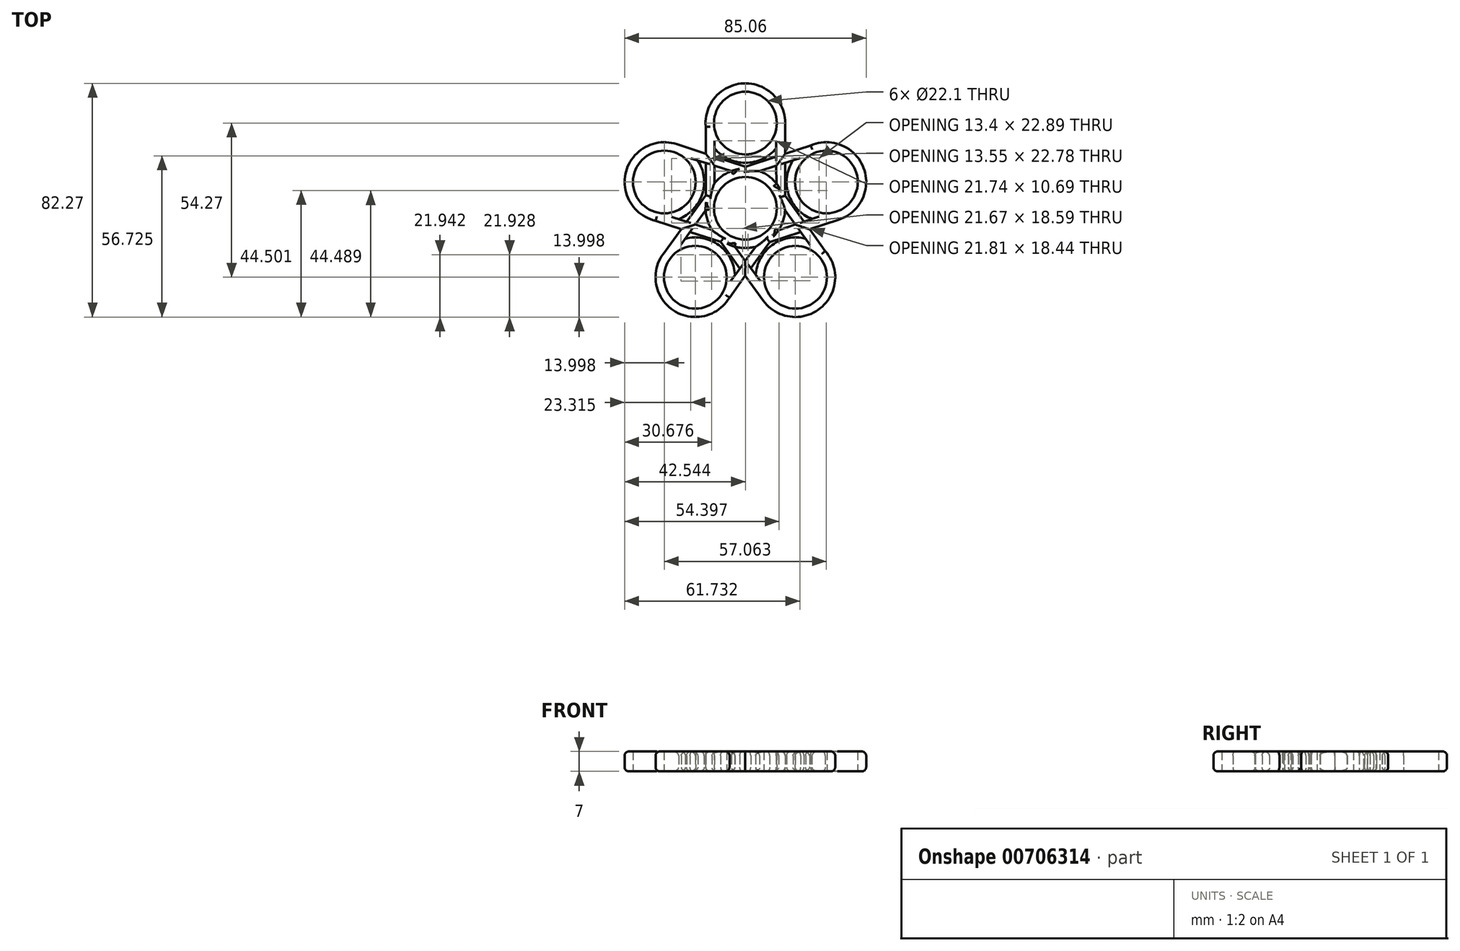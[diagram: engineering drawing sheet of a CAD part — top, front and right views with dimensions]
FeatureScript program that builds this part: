
annotation { "Feature Type Name" : "Feature", "Feature Type Description" : "" }
export const myFeature = defineFeature(function(context is Context, id is Id, definition is map)
    precondition{}
    {
        {
            var Q0;
            Q0=qCreatedBy(makeId("Top.planeOp"),FACE);
            var sketch = newSketch(context, id + "F0", { "sketchPlane" : qUnion([Q0])});
            skCircle(sketch, "E0", {"center": v(0, 22.69) * mm, "radius": 14 * mm});
            skCircle(sketch, "E1", {"center": v(0, 22.69) * mm, "radius": 11.05 * mm});
            skCircle(sketch, "E2", {"center": v(0, -7.31) * mm, "radius": 14 * mm});
            skCircle(sketch, "E3", {"center": v(0, -7.31) * mm, "radius": 11.05 * mm});
            skLineSegment(sketch, "E4", {"start": v(-13.94, 21.4) * mm, "end": v(-13.94, -8.6) * mm});
            skLineSegment(sketch, "E5", {"start": v(14, 22.69) * mm, "end": v(14, -7.31) * mm});
            skLineSegment(sketch, "E6", {"start": v(-10.85, 20.62) * mm, "end": v(-10.85, -9.38) * mm});
            skLineSegment(sketch, "E7", {"start": v(10.77, 20.22) * mm, "end": v(11.05, -7.2) * mm});
            skSolve(sketch);
        }
        {
            var Q0;
            {var subQ0=sQuery(id+"F0.wireOp",EDGE,"E0");var subQ4=makeQuery(id+"F0.imprint","INTERSECT",VERTEX,{"derivedFrom":[subQ0,sQuery(id+"F0.wireOp",EDGE,"E4")]});Q0=makeQuery(id+"F0.imprint","IMPRINT",FACE,{"disambiguationData":[TD([[makeQuery(id+"F0.imprint","IMPRINT",EDGE,{"disambiguationData":[TD([[subQ4,1.0]])],"derivedFrom":subQ0}),1.0]])]});}
            var Q1;
            {var subQ0=sQuery(id+"F0.wireOp",EDGE,"E6");var subQ1=sQuery(id+"F0.wireOp",EDGE,"E0");var subQ2=makeQuery(id+"F0.imprint","INTERSECT",VERTEX,{"derivedFrom":[subQ1,subQ0]});Q1=makeQuery(id+"F0.imprint","IMPRINT",FACE,{"disambiguationData":[TD([[makeQuery(id+"F0.imprint","IMPRINT",EDGE,{"disambiguationData":[TD([[subQ2,-1.0]])],"derivedFrom":subQ1}),1.0]])]});}
            var Q2;
            {var subQ0=sQuery(id+"F0.wireOp",EDGE,"E7");var subQ1=sQuery(id+"F0.wireOp",EDGE,"E2");var subQ2=makeQuery(id+"F0.imprint","INTERSECT",VERTEX,{"derivedFrom":[subQ1,subQ0]});Q2=makeQuery(id+"F0.imprint","IMPRINT",FACE,{"disambiguationData":[TD([[makeQuery(id+"F0.imprint","IMPRINT",EDGE,{"disambiguationData":[TD([[subQ2,-1.0]])],"derivedFrom":subQ1}),1.0]])]});}
            var Q3;
            {var subQ6=sQuery(id+"F0.wireOp",EDGE,"E2");var subQ10=makeQuery(id+"F0.imprint","INTERSECT",VERTEX,{"derivedFrom":[subQ6,sQuery(id+"F0.wireOp",EDGE,"E5")]});Q3=makeQuery(id+"F0.imprint","IMPRINT",FACE,{"disambiguationData":[TD([[makeQuery(id+"F0.imprint","IMPRINT",EDGE,{"disambiguationData":[TD([[subQ10,-1.0]])],"derivedFrom":subQ6}),1.0]])]});}
            var Q4;
            {var subQ0=sQuery(id+"F0.wireOp",EDGE,"E5");Q4=makeQuery(id+"F0.imprint","IMPRINT",FACE,{"disambiguationData":[TD([[makeQuery(id+"F0.imprint","IMPRINT",EDGE,{"derivedFrom":subQ0}),-1.0]])]});}
            var Q5;
            {var subQ0=sQuery(id+"F0.wireOp",EDGE,"E4");var subQ1=sQuery(id+"F0.wireOp",EDGE,"E0");var subQ2=makeQuery(id+"F0.imprint","INTERSECT",VERTEX,{"derivedFrom":[subQ1,subQ0]});Q5=makeQuery(id+"F0.imprint","IMPRINT",FACE,{"disambiguationData":[TD([[makeQuery(id+"F0.imprint","IMPRINT",EDGE,{"disambiguationData":[TD([[subQ2,-1.0]])],"derivedFrom":subQ1}),-1.0]])]});}
            extrude(context, id + "F1", {"entities" : qUnion([Q0, Q1, Q2, Q3, Q4, Q5]), "depth" : 7 * mm, "offsetDistance" : 25 * mm});
        }
        {
            var Q0;
            Q0=makeQuery(id+"F1.opExtrude","SWEPT_BODY",BODY,{"disambiguationData":[OSD([sQuery(id+"F0.wireOp",EDGE,"E0"),sQuery(id+"F0.wireOp",EDGE,"E1"),sQuery(id+"F0.wireOp",EDGE,"E2"),sQuery(id+"F0.wireOp",EDGE,"E3"),sQuery(id+"F0.wireOp",EDGE,"E4"),sQuery(id+"F0.wireOp",EDGE,"E5"),sQuery(id+"F0.wireOp",EDGE,"E6"),sQuery(id+"F0.wireOp",EDGE,"E7")])]});
            var Q1;
            {var subQ0=sQuery(id+"F0.wireOp",EDGE,"E2");Q1=makeQuery(id+"F1.opExtrude","SWEPT_FACE",FACE,{"disambiguationData":[OSD([subQ0]),TDD([makeQuery(id+"F0.imprint","IMPRINT",EDGE,{"disambiguationData":[TD([[makeQuery(id+"F0.imprint","INTERSECT",VERTEX,{"disambiguationData":[OD(0.0)],"derivedFrom":[subQ0,sQuery(id+"F0.wireOp",EDGE,"E4")]}),-1.0]])],"derivedFrom":subQ0})])]});}
            circularPattern(context, id + "F2", {"entities" : qUnion([Q0]), "axis" : qUnion([Q1]), "angle" : 360 * degree, "instanceCount" : 5, "equalSpace" : true});
        }
        {
            var Q0;
            Q0=makeQuery(id+"F1.opExtrude","SWEPT_BODY",BODY,{"disambiguationData":[OSD([sQuery(id+"F0.wireOp",EDGE,"E0"),sQuery(id+"F0.wireOp",EDGE,"E1"),sQuery(id+"F0.wireOp",EDGE,"E2"),sQuery(id+"F0.wireOp",EDGE,"E3"),sQuery(id+"F0.wireOp",EDGE,"E4"),sQuery(id+"F0.wireOp",EDGE,"E5"),sQuery(id+"F0.wireOp",EDGE,"E6"),sQuery(id+"F0.wireOp",EDGE,"E7")])]});
            var Q1;
            Q1=makeQuery(id+"F2.opPattern","COPY",BODY,{"derivedFrom":makeQuery(id+"F1.opExtrude","SWEPT_BODY",BODY,{"disambiguationData":[OSD([sQuery(id+"F0.wireOp",EDGE,"E0"),sQuery(id+"F0.wireOp",EDGE,"E1"),sQuery(id+"F0.wireOp",EDGE,"E2"),sQuery(id+"F0.wireOp",EDGE,"E3"),sQuery(id+"F0.wireOp",EDGE,"E4"),sQuery(id+"F0.wireOp",EDGE,"E5"),sQuery(id+"F0.wireOp",EDGE,"E6"),sQuery(id+"F0.wireOp",EDGE,"E7")])]}),"instanceName":"1"});
            var Q2;
            Q2=makeQuery(id+"F2.opPattern","COPY",BODY,{"derivedFrom":makeQuery(id+"F1.opExtrude","SWEPT_BODY",BODY,{"disambiguationData":[OSD([sQuery(id+"F0.wireOp",EDGE,"E0"),sQuery(id+"F0.wireOp",EDGE,"E1"),sQuery(id+"F0.wireOp",EDGE,"E2"),sQuery(id+"F0.wireOp",EDGE,"E3"),sQuery(id+"F0.wireOp",EDGE,"E4"),sQuery(id+"F0.wireOp",EDGE,"E5"),sQuery(id+"F0.wireOp",EDGE,"E6"),sQuery(id+"F0.wireOp",EDGE,"E7")])]}),"instanceName":"2"});
            var Q3;
            Q3=makeQuery(id+"F2.opPattern","COPY",BODY,{"derivedFrom":makeQuery(id+"F1.opExtrude","SWEPT_BODY",BODY,{"disambiguationData":[OSD([sQuery(id+"F0.wireOp",EDGE,"E0"),sQuery(id+"F0.wireOp",EDGE,"E1"),sQuery(id+"F0.wireOp",EDGE,"E2"),sQuery(id+"F0.wireOp",EDGE,"E3"),sQuery(id+"F0.wireOp",EDGE,"E4"),sQuery(id+"F0.wireOp",EDGE,"E5"),sQuery(id+"F0.wireOp",EDGE,"E6"),sQuery(id+"F0.wireOp",EDGE,"E7")])]}),"instanceName":"3"});
            var Q4;
            Q4=makeQuery(id+"F2.opPattern","COPY",BODY,{"derivedFrom":makeQuery(id+"F1.opExtrude","SWEPT_BODY",BODY,{"disambiguationData":[OSD([sQuery(id+"F0.wireOp",EDGE,"E0"),sQuery(id+"F0.wireOp",EDGE,"E1"),sQuery(id+"F0.wireOp",EDGE,"E2"),sQuery(id+"F0.wireOp",EDGE,"E3"),sQuery(id+"F0.wireOp",EDGE,"E4"),sQuery(id+"F0.wireOp",EDGE,"E5"),sQuery(id+"F0.wireOp",EDGE,"E6"),sQuery(id+"F0.wireOp",EDGE,"E7")])]}),"instanceName":"4"});
            var Q5;
            Q5=makeQuery(id+"F2.opPattern","COPY",BODY,{"derivedFrom":makeQuery(id+"F1.opExtrude","SWEPT_BODY",BODY,{"disambiguationData":[OSD([sQuery(id+"F0.wireOp",EDGE,"E0"),sQuery(id+"F0.wireOp",EDGE,"E1"),sQuery(id+"F0.wireOp",EDGE,"E2"),sQuery(id+"F0.wireOp",EDGE,"E3"),sQuery(id+"F0.wireOp",EDGE,"E4"),sQuery(id+"F0.wireOp",EDGE,"E5"),sQuery(id+"F0.wireOp",EDGE,"E6"),sQuery(id+"F0.wireOp",EDGE,"E7")])]}),"instanceName":"5"});
            booleanBodies(context, id + "F3", {"operationType" : BooleanOperationType.UNION, "tools" : qUnion([Q0, Q1, Q2, Q3, Q4, Q5])});
        }
        {
            var Q0;
            {var subQ0=sQuery(id+"F0.wireOp",EDGE,"E5");var subQ1=sQuery(id+"F0.wireOp",EDGE,"E4");Q0=makeQuery(id+"F3.opBoolean","SPLIT",EDGE,{"disambiguationData":[TD([makeQuery(id+"F2.opPattern","COPY",FACE,{"derivedFrom":makeQuery(id+"F1.opExtrude","SWEPT_FACE",FACE,{"disambiguationData":[OSD([subQ0])]}),"instanceName":"4"})])],"derivedFrom":makeQuery(id+"F1.opExtrude","CAP_EDGE",EDGE,{"disambiguationData":[OSD([subQ1])],"isStart":false})});}
            var Q1;
            {var subQ0=sQuery(id+"F0.wireOp",EDGE,"E0");Q1=makeQuery(id+"F1.opExtrude","CAP_EDGE",EDGE,{"disambiguationData":[OSD([subQ0]),TDD([makeQuery(id+"F0.imprint","IMPRINT",EDGE,{"disambiguationData":[TD([[makeQuery(id+"F0.imprint","INTERSECT",VERTEX,{"derivedFrom":[subQ0,sQuery(id+"F0.wireOp",EDGE,"E4")]}),1.0]])],"derivedFrom":subQ0})])],"isStart":false});}
            var Q2;
            {var subQ0=sQuery(id+"F0.wireOp",EDGE,"E0");Q2=makeQuery(id+"F1.opExtrude","CAP_EDGE",EDGE,{"disambiguationData":[OSD([subQ0]),TDD([makeQuery(id+"F0.imprint","IMPRINT",EDGE,{"disambiguationData":[TD([[makeQuery(id+"F0.imprint","INTERSECT",VERTEX,{"derivedFrom":[subQ0,sQuery(id+"F0.wireOp",EDGE,"E6")]}),-1.0]])],"derivedFrom":subQ0})])],"isStart":false});}
            var Q3;
            {var subQ1=sQuery(id+"F0.wireOp",EDGE,"E6");var subQ2=sQuery(id+"F0.wireOp",EDGE,"E5");Q3=makeQuery(id+"F3.opBoolean","SPLIT",EDGE,{"disambiguationData":[TD([makeQuery(id+"F1.opExtrude","SWEPT_FACE",FACE,{"disambiguationData":[OSD([subQ1])]})])],"derivedFrom":makeQuery(id+"F2.opPattern","COPY",EDGE,{"derivedFrom":makeQuery(id+"F1.opExtrude","CAP_EDGE",EDGE,{"disambiguationData":[OSD([subQ2])],"isStart":false}),"instanceName":"4"})});}
            var Q4;
            {var subQ0=sQuery(id+"F0.wireOp",EDGE,"E4");var subQ1=sQuery(id+"F0.wireOp",EDGE,"E7");Q4=makeQuery(id+"F3.opBoolean","SPLIT",EDGE,{"disambiguationData":[TD([makeQuery(id+"F1.opExtrude","SWEPT_FACE",FACE,{"disambiguationData":[OSD([subQ1])]})])],"derivedFrom":makeQuery(id+"F2.opPattern","COPY",EDGE,{"derivedFrom":makeQuery(id+"F1.opExtrude","CAP_EDGE",EDGE,{"disambiguationData":[OSD([subQ0])],"isStart":false}),"instanceName":"1"})});}
            var Q5;
            {var subQ0=sQuery(id+"F0.wireOp",EDGE,"E5");var subQ1=sQuery(id+"F0.wireOp",EDGE,"E4");Q5=makeQuery(id+"F3.opBoolean","SPLIT",EDGE,{"disambiguationData":[TD([makeQuery(id+"F1.opExtrude","SWEPT_FACE",FACE,{"disambiguationData":[OSD([subQ0])]})])],"derivedFrom":makeQuery(id+"F2.opPattern","COPY",EDGE,{"derivedFrom":makeQuery(id+"F1.opExtrude","CAP_EDGE",EDGE,{"disambiguationData":[OSD([subQ1])],"isStart":false}),"instanceName":"1"})});}
            var Q6;
            {var subQ0=sQuery(id+"F0.wireOp",EDGE,"E0");Q6=makeQuery(id+"F2.opPattern","COPY",EDGE,{"derivedFrom":makeQuery(id+"F1.opExtrude","CAP_EDGE",EDGE,{"disambiguationData":[OSD([subQ0]),TDD([makeQuery(id+"F0.imprint","IMPRINT",EDGE,{"disambiguationData":[TD([[makeQuery(id+"F0.imprint","INTERSECT",VERTEX,{"derivedFrom":[subQ0,sQuery(id+"F0.wireOp",EDGE,"E4")]}),1.0]])],"derivedFrom":subQ0})])],"isStart":false}),"instanceName":"1"});}
            var Q7;
            {var subQ0=sQuery(id+"F0.wireOp",EDGE,"E0");Q7=makeQuery(id+"F2.opPattern","COPY",EDGE,{"derivedFrom":makeQuery(id+"F1.opExtrude","CAP_EDGE",EDGE,{"disambiguationData":[OSD([subQ0]),TDD([makeQuery(id+"F0.imprint","IMPRINT",EDGE,{"disambiguationData":[TD([[makeQuery(id+"F0.imprint","INTERSECT",VERTEX,{"derivedFrom":[subQ0,sQuery(id+"F0.wireOp",EDGE,"E6")]}),-1.0]])],"derivedFrom":subQ0})])],"isStart":false}),"instanceName":"1"});}
            var Q8;
            {var subQ0=sQuery(id+"F0.wireOp",EDGE,"E6");var subQ1=sQuery(id+"F0.wireOp",EDGE,"E5");Q8=makeQuery(id+"F3.opBoolean","SPLIT",EDGE,{"disambiguationData":[TD([makeQuery(id+"F2.opPattern","COPY",FACE,{"derivedFrom":makeQuery(id+"F1.opExtrude","SWEPT_FACE",FACE,{"disambiguationData":[OSD([subQ0])]}),"instanceName":"1"})])],"derivedFrom":makeQuery(id+"F1.opExtrude","CAP_EDGE",EDGE,{"disambiguationData":[OSD([subQ1])],"isStart":false})});}
            var Q9;
            {var subQ1=sQuery(id+"F0.wireOp",EDGE,"E5");var subQ2=sQuery(id+"F0.wireOp",EDGE,"E4");Q9=makeQuery(id+"F3.opBoolean","SPLIT",EDGE,{"disambiguationData":[TD([makeQuery(id+"F1.opExtrude","SWEPT_FACE",FACE,{"disambiguationData":[OSD([subQ1])]})])],"derivedFrom":makeQuery(id+"F2.opPattern","COPY",EDGE,{"derivedFrom":makeQuery(id+"F1.opExtrude","CAP_EDGE",EDGE,{"disambiguationData":[OSD([subQ2])],"isStart":false}),"instanceName":"2"})});}
            var Q10;
            {var subQ0=sQuery(id+"F0.wireOp",EDGE,"E7");var subQ1=sQuery(id+"F0.wireOp",EDGE,"E6");Q10=makeQuery(id+"F3.opBoolean","SPLIT",EDGE,{"disambiguationData":[TD([makeQuery(id+"F2.opPattern","COPY",FACE,{"derivedFrom":makeQuery(id+"F1.opExtrude","SWEPT_FACE",FACE,{"disambiguationData":[OSD([subQ0])]}),"instanceName":"4"})])],"derivedFrom":makeQuery(id+"F1.opExtrude","CAP_EDGE",EDGE,{"disambiguationData":[OSD([subQ1])],"isStart":false})});}
            var Q11;
            {var subQ0=sQuery(id+"F0.wireOp",EDGE,"E7");var subQ1=sQuery(id+"F0.wireOp",EDGE,"E6");Q11=makeQuery(id+"F3.opBoolean","SPLIT",EDGE,{"disambiguationData":[TD([makeQuery(id+"F1.opExtrude","SWEPT_FACE",FACE,{"disambiguationData":[OSD([subQ1])]})])],"derivedFrom":makeQuery(id+"F2.opPattern","COPY",EDGE,{"derivedFrom":makeQuery(id+"F1.opExtrude","CAP_EDGE",EDGE,{"disambiguationData":[OSD([subQ0])],"isStart":false}),"instanceName":"4"})});}
            var Q12;
            {var subQ0=sQuery(id+"F0.wireOp",EDGE,"E7");var subQ1=sQuery(id+"F0.wireOp",EDGE,"E6");Q12=makeQuery(id+"F3.opBoolean","SPLIT",EDGE,{"disambiguationData":[TD([makeQuery(id+"F1.opExtrude","SWEPT_FACE",FACE,{"disambiguationData":[OSD([subQ0])]})])],"derivedFrom":makeQuery(id+"F2.opPattern","COPY",EDGE,{"derivedFrom":makeQuery(id+"F1.opExtrude","CAP_EDGE",EDGE,{"disambiguationData":[OSD([subQ1])],"isStart":false}),"instanceName":"1"})});}
            var Q13;
            {var subQ0=sQuery(id+"F0.wireOp",EDGE,"E7");var subQ1=sQuery(id+"F0.wireOp",EDGE,"E6");Q13=makeQuery(id+"F3.opBoolean","SPLIT",EDGE,{"disambiguationData":[TD([makeQuery(id+"F2.opPattern","COPY",FACE,{"derivedFrom":makeQuery(id+"F1.opExtrude","SWEPT_FACE",FACE,{"disambiguationData":[OSD([subQ1])]}),"instanceName":"1"})])],"derivedFrom":makeQuery(id+"F1.opExtrude","CAP_EDGE",EDGE,{"disambiguationData":[OSD([subQ0])],"isStart":false})});}
            var Q14;
            {var subQ0=sQuery(id+"F0.wireOp",EDGE,"E7");var subQ1=sQuery(id+"F0.wireOp",EDGE,"E6");Q14=makeQuery(id+"F3.opBoolean","SPLIT",EDGE,{"disambiguationData":[TD([makeQuery(id+"F2.opPattern","COPY",FACE,{"derivedFrom":makeQuery(id+"F1.opExtrude","SWEPT_FACE",FACE,{"disambiguationData":[OSD([subQ0])]}),"instanceName":"1"})])],"derivedFrom":makeQuery(id+"F2.opPattern","COPY",EDGE,{"derivedFrom":makeQuery(id+"F1.opExtrude","CAP_EDGE",EDGE,{"disambiguationData":[OSD([subQ1])],"isStart":false}),"instanceName":"2"})});}
            var Q15;
            {var subQ0=sQuery(id+"F0.wireOp",EDGE,"E7");var subQ1=sQuery(id+"F0.wireOp",EDGE,"E6");Q15=makeQuery(id+"F3.opBoolean","SPLIT",EDGE,{"disambiguationData":[TD([makeQuery(id+"F2.opPattern","COPY",FACE,{"derivedFrom":makeQuery(id+"F1.opExtrude","SWEPT_FACE",FACE,{"disambiguationData":[OSD([subQ1])]}),"instanceName":"2"})])],"derivedFrom":makeQuery(id+"F2.opPattern","COPY",EDGE,{"derivedFrom":makeQuery(id+"F1.opExtrude","CAP_EDGE",EDGE,{"disambiguationData":[OSD([subQ0])],"isStart":false}),"instanceName":"1"})});}
            var Q16;
            {var subQ0=sQuery(id+"F0.wireOp",EDGE,"E7");var subQ1=sQuery(id+"F0.wireOp",EDGE,"E6");Q16=makeQuery(id+"F3.opBoolean","SPLIT",EDGE,{"disambiguationData":[TD([makeQuery(id+"F2.opPattern","COPY",FACE,{"derivedFrom":makeQuery(id+"F1.opExtrude","SWEPT_FACE",FACE,{"disambiguationData":[OSD([subQ1])]}),"instanceName":"4"})])],"derivedFrom":makeQuery(id+"F2.opPattern","COPY",EDGE,{"derivedFrom":makeQuery(id+"F1.opExtrude","CAP_EDGE",EDGE,{"disambiguationData":[OSD([subQ0])],"isStart":false}),"instanceName":"3"})});}
            var Q17;
            {var subQ0=sQuery(id+"F0.wireOp",EDGE,"E7");var subQ1=sQuery(id+"F0.wireOp",EDGE,"E6");Q17=makeQuery(id+"F3.opBoolean","SPLIT",EDGE,{"disambiguationData":[TD([makeQuery(id+"F2.opPattern","COPY",FACE,{"derivedFrom":makeQuery(id+"F1.opExtrude","SWEPT_FACE",FACE,{"disambiguationData":[OSD([subQ0])]}),"instanceName":"3"})])],"derivedFrom":makeQuery(id+"F2.opPattern","COPY",EDGE,{"derivedFrom":makeQuery(id+"F1.opExtrude","CAP_EDGE",EDGE,{"disambiguationData":[OSD([subQ1])],"isStart":false}),"instanceName":"4"})});}
            var Q18;
            {var subQ0=sQuery(id+"F0.wireOp",EDGE,"E7");var subQ1=sQuery(id+"F0.wireOp",EDGE,"E6");Q18=makeQuery(id+"F3.opBoolean","SPLIT",EDGE,{"disambiguationData":[TD([makeQuery(id+"F2.opPattern","COPY",FACE,{"derivedFrom":makeQuery(id+"F1.opExtrude","SWEPT_FACE",FACE,{"disambiguationData":[OSD([subQ1])]}),"instanceName":"3"})])],"derivedFrom":makeQuery(id+"F2.opPattern","COPY",EDGE,{"derivedFrom":makeQuery(id+"F1.opExtrude","CAP_EDGE",EDGE,{"disambiguationData":[OSD([subQ0])],"isStart":false}),"instanceName":"2"})});}
            var Q19;
            {var subQ0=sQuery(id+"F0.wireOp",EDGE,"E7");var subQ1=sQuery(id+"F0.wireOp",EDGE,"E6");Q19=makeQuery(id+"F3.opBoolean","SPLIT",EDGE,{"disambiguationData":[TD([makeQuery(id+"F2.opPattern","COPY",FACE,{"derivedFrom":makeQuery(id+"F1.opExtrude","SWEPT_FACE",FACE,{"disambiguationData":[OSD([subQ0])]}),"instanceName":"2"})])],"derivedFrom":makeQuery(id+"F2.opPattern","COPY",EDGE,{"derivedFrom":makeQuery(id+"F1.opExtrude","CAP_EDGE",EDGE,{"disambiguationData":[OSD([subQ1])],"isStart":false}),"instanceName":"3"})});}
            var Q20;
            {var subQ0=sQuery(id+"F0.wireOp",EDGE,"E5");var subQ1=sQuery(id+"F0.wireOp",EDGE,"E4");Q20=makeQuery(id+"F3.opBoolean","SPLIT",EDGE,{"disambiguationData":[TD([makeQuery(id+"F2.opPattern","COPY",FACE,{"derivedFrom":makeQuery(id+"F1.opExtrude","SWEPT_FACE",FACE,{"disambiguationData":[OSD([subQ0])]}),"instanceName":"1"})])],"derivedFrom":makeQuery(id+"F2.opPattern","COPY",EDGE,{"derivedFrom":makeQuery(id+"F1.opExtrude","CAP_EDGE",EDGE,{"disambiguationData":[OSD([subQ1])],"isStart":false}),"instanceName":"2"})});}
            var Q21;
            {var subQ0=sQuery(id+"F0.wireOp",EDGE,"E0");Q21=makeQuery(id+"F2.opPattern","COPY",EDGE,{"derivedFrom":makeQuery(id+"F1.opExtrude","CAP_EDGE",EDGE,{"disambiguationData":[OSD([subQ0]),TDD([makeQuery(id+"F0.imprint","IMPRINT",EDGE,{"disambiguationData":[TD([[makeQuery(id+"F0.imprint","INTERSECT",VERTEX,{"derivedFrom":[subQ0,sQuery(id+"F0.wireOp",EDGE,"E4")]}),1.0]])],"derivedFrom":subQ0})])],"isStart":false}),"instanceName":"2"});}
            var Q22;
            {var subQ0=sQuery(id+"F0.wireOp",EDGE,"E5");var subQ1=sQuery(id+"F0.wireOp",EDGE,"E4");Q22=makeQuery(id+"F3.opBoolean","SPLIT",EDGE,{"disambiguationData":[TD([makeQuery(id+"F2.opPattern","COPY",FACE,{"derivedFrom":makeQuery(id+"F1.opExtrude","SWEPT_FACE",FACE,{"disambiguationData":[OSD([subQ0])]}),"instanceName":"2"})])],"derivedFrom":makeQuery(id+"F2.opPattern","COPY",EDGE,{"derivedFrom":makeQuery(id+"F1.opExtrude","CAP_EDGE",EDGE,{"disambiguationData":[OSD([subQ1])],"isStart":false}),"instanceName":"3"})});}
            var Q23;
            {var subQ0=sQuery(id+"F0.wireOp",EDGE,"E0");Q23=makeQuery(id+"F2.opPattern","COPY",EDGE,{"derivedFrom":makeQuery(id+"F1.opExtrude","CAP_EDGE",EDGE,{"disambiguationData":[OSD([subQ0]),TDD([makeQuery(id+"F0.imprint","IMPRINT",EDGE,{"disambiguationData":[TD([[makeQuery(id+"F0.imprint","INTERSECT",VERTEX,{"derivedFrom":[subQ0,sQuery(id+"F0.wireOp",EDGE,"E4")]}),1.0]])],"derivedFrom":subQ0})])],"isStart":false}),"instanceName":"3"});}
            var Q24;
            {var subQ0=sQuery(id+"F0.wireOp",EDGE,"E5");var subQ1=sQuery(id+"F0.wireOp",EDGE,"E4");Q24=makeQuery(id+"F3.opBoolean","SPLIT",EDGE,{"disambiguationData":[TD([makeQuery(id+"F2.opPattern","COPY",FACE,{"derivedFrom":makeQuery(id+"F1.opExtrude","SWEPT_FACE",FACE,{"disambiguationData":[OSD([subQ0])]}),"instanceName":"3"})])],"derivedFrom":makeQuery(id+"F2.opPattern","COPY",EDGE,{"derivedFrom":makeQuery(id+"F1.opExtrude","CAP_EDGE",EDGE,{"disambiguationData":[OSD([subQ1])],"isStart":false}),"instanceName":"4"})});}
            var Q25;
            {var subQ0=sQuery(id+"F0.wireOp",EDGE,"E0");Q25=makeQuery(id+"F2.opPattern","COPY",EDGE,{"derivedFrom":makeQuery(id+"F1.opExtrude","CAP_EDGE",EDGE,{"disambiguationData":[OSD([subQ0]),TDD([makeQuery(id+"F0.imprint","IMPRINT",EDGE,{"disambiguationData":[TD([[makeQuery(id+"F0.imprint","INTERSECT",VERTEX,{"derivedFrom":[subQ0,sQuery(id+"F0.wireOp",EDGE,"E4")]}),1.0]])],"derivedFrom":subQ0})])],"isStart":false}),"instanceName":"4"});}
            var Q26;
            {var subQ0=sQuery(id+"F0.wireOp",EDGE,"E0");Q26=makeQuery(id+"F2.opPattern","COPY",EDGE,{"derivedFrom":makeQuery(id+"F1.opExtrude","CAP_EDGE",EDGE,{"disambiguationData":[OSD([subQ0]),TDD([makeQuery(id+"F0.imprint","IMPRINT",EDGE,{"disambiguationData":[TD([[makeQuery(id+"F0.imprint","INTERSECT",VERTEX,{"derivedFrom":[subQ0,sQuery(id+"F0.wireOp",EDGE,"E6")]}),-1.0]])],"derivedFrom":subQ0})])],"isStart":false}),"instanceName":"4"});}
            var Q27;
            {var subQ1=sQuery(id+"F0.wireOp",EDGE,"E5");var subQ2=sQuery(id+"F0.wireOp",EDGE,"E4");Q27=makeQuery(id+"F3.opBoolean","SPLIT",EDGE,{"disambiguationData":[TD([makeQuery(id+"F2.opPattern","COPY",FACE,{"derivedFrom":makeQuery(id+"F1.opExtrude","SWEPT_FACE",FACE,{"disambiguationData":[OSD([subQ1])]}),"instanceName":"3"})])],"derivedFrom":makeQuery(id+"F1.opExtrude","CAP_EDGE",EDGE,{"disambiguationData":[OSD([subQ2])],"isStart":false})});}
            var Q28;
            {var subQ1=sQuery(id+"F0.wireOp",EDGE,"E5");var subQ2=sQuery(id+"F0.wireOp",EDGE,"E4");Q28=makeQuery(id+"F3.opBoolean","SPLIT",EDGE,{"disambiguationData":[TD([makeQuery(id+"F1.opExtrude","SWEPT_FACE",FACE,{"disambiguationData":[OSD([subQ2])]})])],"derivedFrom":makeQuery(id+"F2.opPattern","COPY",EDGE,{"derivedFrom":makeQuery(id+"F1.opExtrude","CAP_EDGE",EDGE,{"disambiguationData":[OSD([subQ1])],"isStart":false}),"instanceName":"3"})});}
            var Q29;
            {var subQ0=sQuery(id+"F0.wireOp",EDGE,"E0");Q29=makeQuery(id+"F2.opPattern","COPY",EDGE,{"derivedFrom":makeQuery(id+"F1.opExtrude","CAP_EDGE",EDGE,{"disambiguationData":[OSD([subQ0]),TDD([makeQuery(id+"F0.imprint","IMPRINT",EDGE,{"disambiguationData":[TD([[makeQuery(id+"F0.imprint","INTERSECT",VERTEX,{"derivedFrom":[subQ0,sQuery(id+"F0.wireOp",EDGE,"E6")]}),-1.0]])],"derivedFrom":subQ0})])],"isStart":false}),"instanceName":"2"});}
            var Q30;
            {var subQ1=sQuery(id+"F0.wireOp",EDGE,"E5");var subQ2=sQuery(id+"F0.wireOp",EDGE,"E4");Q30=makeQuery(id+"F3.opBoolean","SPLIT",EDGE,{"disambiguationData":[TD([makeQuery(id+"F2.opPattern","COPY",FACE,{"derivedFrom":makeQuery(id+"F1.opExtrude","SWEPT_FACE",FACE,{"disambiguationData":[OSD([subQ1])]}),"instanceName":"1"})])],"derivedFrom":makeQuery(id+"F2.opPattern","COPY",EDGE,{"derivedFrom":makeQuery(id+"F1.opExtrude","CAP_EDGE",EDGE,{"disambiguationData":[OSD([subQ2])],"isStart":false}),"instanceName":"3"})});}
            var Q31;
            {var subQ0=sQuery(id+"F0.wireOp",EDGE,"E6");var subQ1=sQuery(id+"F0.wireOp",EDGE,"E5");Q31=makeQuery(id+"F3.opBoolean","SPLIT",EDGE,{"disambiguationData":[TD([makeQuery(id+"F2.opPattern","COPY",FACE,{"derivedFrom":makeQuery(id+"F1.opExtrude","SWEPT_FACE",FACE,{"disambiguationData":[OSD([subQ0])]}),"instanceName":"2"})])],"derivedFrom":makeQuery(id+"F2.opPattern","COPY",EDGE,{"derivedFrom":makeQuery(id+"F1.opExtrude","CAP_EDGE",EDGE,{"disambiguationData":[OSD([subQ1])],"isStart":false}),"instanceName":"1"})});}
            var Q32;
            {var subQ0=sQuery(id+"F0.wireOp",EDGE,"E0");Q32=makeQuery(id+"F2.opPattern","COPY",EDGE,{"derivedFrom":makeQuery(id+"F1.opExtrude","CAP_EDGE",EDGE,{"disambiguationData":[OSD([subQ0]),TDD([makeQuery(id+"F0.imprint","IMPRINT",EDGE,{"disambiguationData":[TD([[makeQuery(id+"F0.imprint","INTERSECT",VERTEX,{"derivedFrom":[subQ0,sQuery(id+"F0.wireOp",EDGE,"E6")]}),-1.0]])],"derivedFrom":subQ0})])],"isStart":false}),"instanceName":"3"});}
            var Q33;
            {var subQ1=sQuery(id+"F0.wireOp",EDGE,"E5");var subQ2=sQuery(id+"F0.wireOp",EDGE,"E4");Q33=makeQuery(id+"F3.opBoolean","SPLIT",EDGE,{"disambiguationData":[TD([makeQuery(id+"F2.opPattern","COPY",FACE,{"derivedFrom":makeQuery(id+"F1.opExtrude","SWEPT_FACE",FACE,{"disambiguationData":[OSD([subQ1])]}),"instanceName":"2"})])],"derivedFrom":makeQuery(id+"F2.opPattern","COPY",EDGE,{"derivedFrom":makeQuery(id+"F1.opExtrude","CAP_EDGE",EDGE,{"disambiguationData":[OSD([subQ2])],"isStart":false}),"instanceName":"4"})});}
            var Q34;
            {var subQ0=sQuery(id+"F0.wireOp",EDGE,"E6");var subQ1=sQuery(id+"F0.wireOp",EDGE,"E5");Q34=makeQuery(id+"F3.opBoolean","SPLIT",EDGE,{"disambiguationData":[TD([makeQuery(id+"F2.opPattern","COPY",FACE,{"derivedFrom":makeQuery(id+"F1.opExtrude","SWEPT_FACE",FACE,{"disambiguationData":[OSD([subQ0])]}),"instanceName":"3"})])],"derivedFrom":makeQuery(id+"F2.opPattern","COPY",EDGE,{"derivedFrom":makeQuery(id+"F1.opExtrude","CAP_EDGE",EDGE,{"disambiguationData":[OSD([subQ1])],"isStart":false}),"instanceName":"2"})});}
            fillet(context, id + "F4", {"entities" : qUnion([Q0, Q1, Q2, Q3, Q4, Q5, Q6, Q7, Q8, Q9, Q10, Q11, Q12, Q13, Q14, Q15, Q16, Q17, Q18, Q19, Q20, Q21, Q22, Q23, Q24, Q25, Q26, Q27, Q28, Q29, Q30, Q31, Q32, Q33, Q34]), "radius" : 1.5 * mm, "tangentPropagation" : true, "allowEdgeOverflow" : false});
        }
        {
            var Q0;
            {var subQ0=sQuery(id+"F0.wireOp",EDGE,"E7");var subQ1=sQuery(id+"F0.wireOp",EDGE,"E6");var subQ2=sQuery(id+"F0.wireOp",EDGE,"E2");var subQ4=makeQuery(id+"F0.imprint","IMPRINT",EDGE,{"disambiguationData":[TD([[makeQuery(id+"F0.imprint","INTERSECT",VERTEX,{"derivedFrom":[subQ2,subQ0]}),-1.0]])],"derivedFrom":subQ2});Q0=makeQuery(id+"F3.opBoolean","SPLIT",EDGE,{"disambiguationData":[TD([makeQuery(id+"F1.opExtrude","SWEPT_FACE",FACE,{"disambiguationData":[OSD([subQ1])]})])],"derivedFrom":makeQuery(id+"F1.opExtrude","CAP_EDGE",EDGE,{"disambiguationData":[OSD([subQ2]),TDD([subQ4])],"isStart":false})});}
            var Q1;
            {var subQ0=sQuery(id+"F0.wireOp",EDGE,"E7");var subQ2=sQuery(id+"F0.wireOp",EDGE,"E2");var subQ4=makeQuery(id+"F0.imprint","IMPRINT",EDGE,{"disambiguationData":[TD([[makeQuery(id+"F0.imprint","INTERSECT",VERTEX,{"derivedFrom":[subQ2,subQ0]}),-1.0]])],"derivedFrom":subQ2});Q1=makeQuery(id+"F3.opBoolean","SPLIT",EDGE,{"disambiguationData":[TD([makeQuery(id+"F1.opExtrude","SWEPT_FACE",FACE,{"disambiguationData":[OSD([subQ0])]})])],"derivedFrom":makeQuery(id+"F1.opExtrude","CAP_EDGE",EDGE,{"disambiguationData":[OSD([subQ2]),TDD([subQ4])],"isStart":false})});}
            var Q2;
            {var subQ0=sQuery(id+"F0.wireOp",EDGE,"E7");var subQ3=sQuery(id+"F0.wireOp",EDGE,"E4");var subQ4=sQuery(id+"F0.wireOp",EDGE,"E2");var subQ6=makeQuery(id+"F0.imprint","IMPRINT",EDGE,{"disambiguationData":[TD([[makeQuery(id+"F0.imprint","INTERSECT",VERTEX,{"disambiguationData":[OD(0.0)],"derivedFrom":[subQ4,subQ3]}),-1.0]])],"derivedFrom":subQ4});Q2=makeQuery(id+"F3.opBoolean","SPLIT",EDGE,{"disambiguationData":[TD([makeQuery(id+"F2.opPattern","COPY",FACE,{"derivedFrom":makeQuery(id+"F1.opExtrude","SWEPT_FACE",FACE,{"disambiguationData":[OSD([subQ0])]}),"instanceName":"1"})])],"derivedFrom":makeQuery(id+"F1.opExtrude","CAP_EDGE",EDGE,{"disambiguationData":[OSD([subQ4]),TDD([subQ6])],"isStart":false})});}
            var Q3;
            {var subQ0=sQuery(id+"F0.wireOp",EDGE,"E7");var subQ3=sQuery(id+"F0.wireOp",EDGE,"E4");var subQ4=sQuery(id+"F0.wireOp",EDGE,"E2");var subQ6=makeQuery(id+"F0.imprint","IMPRINT",EDGE,{"disambiguationData":[TD([[makeQuery(id+"F0.imprint","INTERSECT",VERTEX,{"disambiguationData":[OD(0.0)],"derivedFrom":[subQ4,subQ3]}),-1.0]])],"derivedFrom":subQ4});Q3=makeQuery(id+"F3.opBoolean","SPLIT",EDGE,{"disambiguationData":[TD([makeQuery(id+"F2.opPattern","COPY",FACE,{"derivedFrom":makeQuery(id+"F1.opExtrude","SWEPT_FACE",FACE,{"disambiguationData":[OSD([subQ0])]}),"instanceName":"2"})])],"derivedFrom":makeQuery(id+"F1.opExtrude","CAP_EDGE",EDGE,{"disambiguationData":[OSD([subQ4]),TDD([subQ6])],"isStart":false})});}
            var Q4;
            {var subQ0=sQuery(id+"F0.wireOp",EDGE,"E2");var subQ1=makeQuery(id+"F1.opExtrude","CAP_EDGE",EDGE,{"disambiguationData":[OSD([subQ0]),TDD([makeQuery(id+"F0.imprint","IMPRINT",EDGE,{"disambiguationData":[TD([[makeQuery(id+"F0.imprint","INTERSECT",VERTEX,{"disambiguationData":[OD(0.0)],"derivedFrom":[subQ0,sQuery(id+"F0.wireOp",EDGE,"E4")]}),-1.0]])],"derivedFrom":subQ0})])],"isStart":false});Q4=makeQuery(id+"F3.opBoolean","MERGE",EDGE,{"derivedFrom":[subQ1,makeQuery(id+"F2.opPattern","COPY",EDGE,{"derivedFrom":subQ1,"instanceName":"1"})]});}
            fillet(context, id + "F5", {"entities" : qUnion([Q0, Q1, Q2, Q3, Q4]), "radius" : 1.2 * mm, "tangentPropagation" : true, "allowEdgeOverflow" : false});
        }
        {
            var Q0;
            {var subQ0=sQuery(id+"F0.wireOp",EDGE,"E4");var subQ2=sQuery(id+"F0.wireOp",EDGE,"E5");Q0=makeQuery(id+"F3.opBoolean","SPLIT",EDGE,{"disambiguationData":[TD([makeQuery(id+"F2.opPattern","COPY",FACE,{"derivedFrom":makeQuery(id+"F1.opExtrude","SWEPT_FACE",FACE,{"disambiguationData":[OSD([subQ0])]}),"instanceName":"4"})])],"derivedFrom":makeQuery(id+"F2.opPattern","COPY",EDGE,{"derivedFrom":makeQuery(id+"F1.opExtrude","CAP_EDGE",EDGE,{"disambiguationData":[OSD([subQ2])],"isStart":true}),"instanceName":"3"})});}
            var Q1;
            {var subQ0=sQuery(id+"F0.wireOp",EDGE,"E0");Q1=makeQuery(id+"F2.opPattern","COPY",EDGE,{"derivedFrom":makeQuery(id+"F1.opExtrude","CAP_EDGE",EDGE,{"disambiguationData":[OSD([subQ0]),TDD([makeQuery(id+"F0.imprint","IMPRINT",EDGE,{"disambiguationData":[TD([[makeQuery(id+"F0.imprint","INTERSECT",VERTEX,{"derivedFrom":[subQ0,sQuery(id+"F0.wireOp",EDGE,"E4")]}),1.0]])],"derivedFrom":subQ0})])],"isStart":true}),"instanceName":"3"});}
            var Q2;
            {var subQ0=sQuery(id+"F0.wireOp",EDGE,"E5");var subQ1=sQuery(id+"F0.wireOp",EDGE,"E4");Q2=makeQuery(id+"F3.opBoolean","SPLIT",EDGE,{"disambiguationData":[TD([makeQuery(id+"F2.opPattern","COPY",FACE,{"derivedFrom":makeQuery(id+"F1.opExtrude","SWEPT_FACE",FACE,{"disambiguationData":[OSD([subQ0])]}),"instanceName":"2"})])],"derivedFrom":makeQuery(id+"F2.opPattern","COPY",EDGE,{"derivedFrom":makeQuery(id+"F1.opExtrude","CAP_EDGE",EDGE,{"disambiguationData":[OSD([subQ1])],"isStart":true}),"instanceName":"3"})});}
            var Q3;
            {var subQ0=sQuery(id+"F0.wireOp",EDGE,"E5");var subQ1=sQuery(id+"F0.wireOp",EDGE,"E4");Q3=makeQuery(id+"F3.opBoolean","SPLIT",EDGE,{"disambiguationData":[TD([makeQuery(id+"F2.opPattern","COPY",FACE,{"derivedFrom":makeQuery(id+"F1.opExtrude","SWEPT_FACE",FACE,{"disambiguationData":[OSD([subQ1])]}),"instanceName":"3"})])],"derivedFrom":makeQuery(id+"F2.opPattern","COPY",EDGE,{"derivedFrom":makeQuery(id+"F1.opExtrude","CAP_EDGE",EDGE,{"disambiguationData":[OSD([subQ0])],"isStart":true}),"instanceName":"2"})});}
            var Q4;
            {var subQ0=sQuery(id+"F0.wireOp",EDGE,"E0");Q4=makeQuery(id+"F2.opPattern","COPY",EDGE,{"derivedFrom":makeQuery(id+"F1.opExtrude","CAP_EDGE",EDGE,{"disambiguationData":[OSD([subQ0]),TDD([makeQuery(id+"F0.imprint","IMPRINT",EDGE,{"disambiguationData":[TD([[makeQuery(id+"F0.imprint","INTERSECT",VERTEX,{"derivedFrom":[subQ0,sQuery(id+"F0.wireOp",EDGE,"E4")]}),1.0]])],"derivedFrom":subQ0})])],"isStart":true}),"instanceName":"2"});}
            var Q5;
            {var subQ0=sQuery(id+"F0.wireOp",EDGE,"E4");var subQ2=sQuery(id+"F0.wireOp",EDGE,"E5");Q5=makeQuery(id+"F3.opBoolean","SPLIT",EDGE,{"disambiguationData":[TD([makeQuery(id+"F2.opPattern","COPY",FACE,{"derivedFrom":makeQuery(id+"F1.opExtrude","SWEPT_FACE",FACE,{"disambiguationData":[OSD([subQ2])]}),"instanceName":"1"})])],"derivedFrom":makeQuery(id+"F2.opPattern","COPY",EDGE,{"derivedFrom":makeQuery(id+"F1.opExtrude","CAP_EDGE",EDGE,{"disambiguationData":[OSD([subQ0])],"isStart":true}),"instanceName":"2"})});}
            var Q6;
            {var subQ0=sQuery(id+"F0.wireOp",EDGE,"E5");var subQ1=sQuery(id+"F0.wireOp",EDGE,"E4");Q6=makeQuery(id+"F3.opBoolean","SPLIT",EDGE,{"disambiguationData":[TD([makeQuery(id+"F2.opPattern","COPY",FACE,{"derivedFrom":makeQuery(id+"F1.opExtrude","SWEPT_FACE",FACE,{"disambiguationData":[OSD([subQ1])]}),"instanceName":"2"})])],"derivedFrom":makeQuery(id+"F2.opPattern","COPY",EDGE,{"derivedFrom":makeQuery(id+"F1.opExtrude","CAP_EDGE",EDGE,{"disambiguationData":[OSD([subQ0])],"isStart":true}),"instanceName":"1"})});}
            var Q7;
            {var subQ0=sQuery(id+"F0.wireOp",EDGE,"E0");Q7=makeQuery(id+"F2.opPattern","COPY",EDGE,{"derivedFrom":makeQuery(id+"F1.opExtrude","CAP_EDGE",EDGE,{"disambiguationData":[OSD([subQ0]),TDD([makeQuery(id+"F0.imprint","IMPRINT",EDGE,{"disambiguationData":[TD([[makeQuery(id+"F0.imprint","INTERSECT",VERTEX,{"derivedFrom":[subQ0,sQuery(id+"F0.wireOp",EDGE,"E4")]}),1.0]])],"derivedFrom":subQ0})])],"isStart":true}),"instanceName":"1"});}
            var Q8;
            {var subQ0=sQuery(id+"F0.wireOp",EDGE,"E5");var subQ1=sQuery(id+"F0.wireOp",EDGE,"E4");Q8=makeQuery(id+"F3.opBoolean","SPLIT",EDGE,{"disambiguationData":[TD([makeQuery(id+"F1.opExtrude","SWEPT_FACE",FACE,{"disambiguationData":[OSD([subQ0])]})])],"derivedFrom":makeQuery(id+"F2.opPattern","COPY",EDGE,{"derivedFrom":makeQuery(id+"F1.opExtrude","CAP_EDGE",EDGE,{"disambiguationData":[OSD([subQ1])],"isStart":true}),"instanceName":"1"})});}
            var Q9;
            {var subQ0=sQuery(id+"F0.wireOp",EDGE,"E5");var subQ1=sQuery(id+"F0.wireOp",EDGE,"E4");Q9=makeQuery(id+"F3.opBoolean","SPLIT",EDGE,{"disambiguationData":[TD([makeQuery(id+"F2.opPattern","COPY",FACE,{"derivedFrom":makeQuery(id+"F1.opExtrude","SWEPT_FACE",FACE,{"disambiguationData":[OSD([subQ0])]}),"instanceName":"3"})])],"derivedFrom":makeQuery(id+"F2.opPattern","COPY",EDGE,{"derivedFrom":makeQuery(id+"F1.opExtrude","CAP_EDGE",EDGE,{"disambiguationData":[OSD([subQ1])],"isStart":true}),"instanceName":"4"})});}
            var Q10;
            {var subQ0=sQuery(id+"F0.wireOp",EDGE,"E0");Q10=makeQuery(id+"F2.opPattern","COPY",EDGE,{"derivedFrom":makeQuery(id+"F1.opExtrude","CAP_EDGE",EDGE,{"disambiguationData":[OSD([subQ0]),TDD([makeQuery(id+"F0.imprint","IMPRINT",EDGE,{"disambiguationData":[TD([[makeQuery(id+"F0.imprint","INTERSECT",VERTEX,{"derivedFrom":[subQ0,sQuery(id+"F0.wireOp",EDGE,"E4")]}),1.0]])],"derivedFrom":subQ0})])],"isStart":true}),"instanceName":"4"});}
            var Q11;
            {var subQ0=sQuery(id+"F0.wireOp",EDGE,"E0");Q11=makeQuery(id+"F1.opExtrude","CAP_EDGE",EDGE,{"disambiguationData":[OSD([subQ0]),TDD([makeQuery(id+"F0.imprint","IMPRINT",EDGE,{"disambiguationData":[TD([[makeQuery(id+"F0.imprint","INTERSECT",VERTEX,{"derivedFrom":[subQ0,sQuery(id+"F0.wireOp",EDGE,"E4")]}),1.0]])],"derivedFrom":subQ0})])],"isStart":true});}
            var Q12;
            {var subQ0=sQuery(id+"F0.wireOp",EDGE,"E5");var subQ1=sQuery(id+"F0.wireOp",EDGE,"E4");Q12=makeQuery(id+"F3.opBoolean","SPLIT",EDGE,{"disambiguationData":[TD([makeQuery(id+"F2.opPattern","COPY",FACE,{"derivedFrom":makeQuery(id+"F1.opExtrude","SWEPT_FACE",FACE,{"disambiguationData":[OSD([subQ0])]}),"instanceName":"4"})])],"derivedFrom":makeQuery(id+"F1.opExtrude","CAP_EDGE",EDGE,{"disambiguationData":[OSD([subQ1])],"isStart":true})});}
            var Q13;
            {var subQ0=sQuery(id+"F0.wireOp",EDGE,"E0");Q13=makeQuery(id+"F2.opPattern","COPY",EDGE,{"derivedFrom":makeQuery(id+"F1.opExtrude","CAP_EDGE",EDGE,{"disambiguationData":[OSD([subQ0]),TDD([makeQuery(id+"F0.imprint","IMPRINT",EDGE,{"disambiguationData":[TD([[makeQuery(id+"F0.imprint","INTERSECT",VERTEX,{"derivedFrom":[subQ0,sQuery(id+"F0.wireOp",EDGE,"E6")]}),-1.0]])],"derivedFrom":subQ0})])],"isStart":true}),"instanceName":"3"});}
            var Q14;
            {var subQ1=sQuery(id+"F0.wireOp",EDGE,"E5");var subQ2=sQuery(id+"F0.wireOp",EDGE,"E4");Q14=makeQuery(id+"F3.opBoolean","SPLIT",EDGE,{"disambiguationData":[TD([makeQuery(id+"F2.opPattern","COPY",FACE,{"derivedFrom":makeQuery(id+"F1.opExtrude","SWEPT_FACE",FACE,{"disambiguationData":[OSD([subQ1])]}),"instanceName":"2"})])],"derivedFrom":makeQuery(id+"F2.opPattern","COPY",EDGE,{"derivedFrom":makeQuery(id+"F1.opExtrude","CAP_EDGE",EDGE,{"disambiguationData":[OSD([subQ2])],"isStart":true}),"instanceName":"4"})});}
            var Q15;
            {var subQ0=sQuery(id+"F0.wireOp",EDGE,"E6");var subQ1=sQuery(id+"F0.wireOp",EDGE,"E5");Q15=makeQuery(id+"F3.opBoolean","SPLIT",EDGE,{"disambiguationData":[TD([makeQuery(id+"F2.opPattern","COPY",FACE,{"derivedFrom":makeQuery(id+"F1.opExtrude","SWEPT_FACE",FACE,{"disambiguationData":[OSD([subQ0])]}),"instanceName":"3"})])],"derivedFrom":makeQuery(id+"F2.opPattern","COPY",EDGE,{"derivedFrom":makeQuery(id+"F1.opExtrude","CAP_EDGE",EDGE,{"disambiguationData":[OSD([subQ1])],"isStart":true}),"instanceName":"2"})});}
            var Q16;
            {var subQ0=sQuery(id+"F0.wireOp",EDGE,"E0");Q16=makeQuery(id+"F2.opPattern","COPY",EDGE,{"derivedFrom":makeQuery(id+"F1.opExtrude","CAP_EDGE",EDGE,{"disambiguationData":[OSD([subQ0]),TDD([makeQuery(id+"F0.imprint","IMPRINT",EDGE,{"disambiguationData":[TD([[makeQuery(id+"F0.imprint","INTERSECT",VERTEX,{"derivedFrom":[subQ0,sQuery(id+"F0.wireOp",EDGE,"E6")]}),-1.0]])],"derivedFrom":subQ0})])],"isStart":true}),"instanceName":"2"});}
            var Q17;
            {var subQ1=sQuery(id+"F0.wireOp",EDGE,"E5");var subQ2=sQuery(id+"F0.wireOp",EDGE,"E4");Q17=makeQuery(id+"F3.opBoolean","SPLIT",EDGE,{"disambiguationData":[TD([makeQuery(id+"F2.opPattern","COPY",FACE,{"derivedFrom":makeQuery(id+"F1.opExtrude","SWEPT_FACE",FACE,{"disambiguationData":[OSD([subQ1])]}),"instanceName":"1"})])],"derivedFrom":makeQuery(id+"F2.opPattern","COPY",EDGE,{"derivedFrom":makeQuery(id+"F1.opExtrude","CAP_EDGE",EDGE,{"disambiguationData":[OSD([subQ2])],"isStart":true}),"instanceName":"3"})});}
            var Q18;
            {var subQ0=sQuery(id+"F0.wireOp",EDGE,"E6");var subQ1=sQuery(id+"F0.wireOp",EDGE,"E5");Q18=makeQuery(id+"F3.opBoolean","SPLIT",EDGE,{"disambiguationData":[TD([makeQuery(id+"F2.opPattern","COPY",FACE,{"derivedFrom":makeQuery(id+"F1.opExtrude","SWEPT_FACE",FACE,{"disambiguationData":[OSD([subQ0])]}),"instanceName":"2"})])],"derivedFrom":makeQuery(id+"F2.opPattern","COPY",EDGE,{"derivedFrom":makeQuery(id+"F1.opExtrude","CAP_EDGE",EDGE,{"disambiguationData":[OSD([subQ1])],"isStart":true}),"instanceName":"1"})});}
            var Q19;
            {var subQ1=sQuery(id+"F0.wireOp",EDGE,"E5");var subQ2=sQuery(id+"F0.wireOp",EDGE,"E4");Q19=makeQuery(id+"F3.opBoolean","SPLIT",EDGE,{"disambiguationData":[TD([makeQuery(id+"F1.opExtrude","SWEPT_FACE",FACE,{"disambiguationData":[OSD([subQ1])]})])],"derivedFrom":makeQuery(id+"F2.opPattern","COPY",EDGE,{"derivedFrom":makeQuery(id+"F1.opExtrude","CAP_EDGE",EDGE,{"disambiguationData":[OSD([subQ2])],"isStart":true}),"instanceName":"2"})});}
            var Q20;
            {var subQ0=sQuery(id+"F0.wireOp",EDGE,"E6");var subQ1=sQuery(id+"F0.wireOp",EDGE,"E5");Q20=makeQuery(id+"F3.opBoolean","SPLIT",EDGE,{"disambiguationData":[TD([makeQuery(id+"F2.opPattern","COPY",FACE,{"derivedFrom":makeQuery(id+"F1.opExtrude","SWEPT_FACE",FACE,{"disambiguationData":[OSD([subQ0])]}),"instanceName":"1"})])],"derivedFrom":makeQuery(id+"F1.opExtrude","CAP_EDGE",EDGE,{"disambiguationData":[OSD([subQ1])],"isStart":true})});}
            var Q21;
            {var subQ0=sQuery(id+"F0.wireOp",EDGE,"E0");Q21=makeQuery(id+"F2.opPattern","COPY",EDGE,{"derivedFrom":makeQuery(id+"F1.opExtrude","CAP_EDGE",EDGE,{"disambiguationData":[OSD([subQ0]),TDD([makeQuery(id+"F0.imprint","IMPRINT",EDGE,{"disambiguationData":[TD([[makeQuery(id+"F0.imprint","INTERSECT",VERTEX,{"derivedFrom":[subQ0,sQuery(id+"F0.wireOp",EDGE,"E6")]}),-1.0]])],"derivedFrom":subQ0})])],"isStart":true}),"instanceName":"1"});}
            var Q22;
            {var subQ0=sQuery(id+"F0.wireOp",EDGE,"E0");Q22=makeQuery(id+"F1.opExtrude","CAP_EDGE",EDGE,{"disambiguationData":[OSD([subQ0]),TDD([makeQuery(id+"F0.imprint","IMPRINT",EDGE,{"disambiguationData":[TD([[makeQuery(id+"F0.imprint","INTERSECT",VERTEX,{"derivedFrom":[subQ0,sQuery(id+"F0.wireOp",EDGE,"E6")]}),-1.0]])],"derivedFrom":subQ0})])],"isStart":true});}
            var Q23;
            {var subQ0=sQuery(id+"F0.wireOp",EDGE,"E4");var subQ1=sQuery(id+"F0.wireOp",EDGE,"E7");Q23=makeQuery(id+"F3.opBoolean","SPLIT",EDGE,{"disambiguationData":[TD([makeQuery(id+"F1.opExtrude","SWEPT_FACE",FACE,{"disambiguationData":[OSD([subQ1])]})])],"derivedFrom":makeQuery(id+"F2.opPattern","COPY",EDGE,{"derivedFrom":makeQuery(id+"F1.opExtrude","CAP_EDGE",EDGE,{"disambiguationData":[OSD([subQ0])],"isStart":true}),"instanceName":"1"})});}
            var Q24;
            {var subQ1=sQuery(id+"F0.wireOp",EDGE,"E6");var subQ2=sQuery(id+"F0.wireOp",EDGE,"E5");Q24=makeQuery(id+"F3.opBoolean","SPLIT",EDGE,{"disambiguationData":[TD([makeQuery(id+"F1.opExtrude","SWEPT_FACE",FACE,{"disambiguationData":[OSD([subQ1])]})])],"derivedFrom":makeQuery(id+"F2.opPattern","COPY",EDGE,{"derivedFrom":makeQuery(id+"F1.opExtrude","CAP_EDGE",EDGE,{"disambiguationData":[OSD([subQ2])],"isStart":true}),"instanceName":"4"})});}
            var Q25;
            {var subQ0=sQuery(id+"F0.wireOp",EDGE,"E0");Q25=makeQuery(id+"F2.opPattern","COPY",EDGE,{"derivedFrom":makeQuery(id+"F1.opExtrude","CAP_EDGE",EDGE,{"disambiguationData":[OSD([subQ0]),TDD([makeQuery(id+"F0.imprint","IMPRINT",EDGE,{"disambiguationData":[TD([[makeQuery(id+"F0.imprint","INTERSECT",VERTEX,{"derivedFrom":[subQ0,sQuery(id+"F0.wireOp",EDGE,"E6")]}),-1.0]])],"derivedFrom":subQ0})])],"isStart":true}),"instanceName":"4"});}
            var Q26;
            {var subQ1=sQuery(id+"F0.wireOp",EDGE,"E5");var subQ2=sQuery(id+"F0.wireOp",EDGE,"E4");Q26=makeQuery(id+"F3.opBoolean","SPLIT",EDGE,{"disambiguationData":[TD([makeQuery(id+"F2.opPattern","COPY",FACE,{"derivedFrom":makeQuery(id+"F1.opExtrude","SWEPT_FACE",FACE,{"disambiguationData":[OSD([subQ1])]}),"instanceName":"3"})])],"derivedFrom":makeQuery(id+"F1.opExtrude","CAP_EDGE",EDGE,{"disambiguationData":[OSD([subQ2])],"isStart":true})});}
            var Q27;
            {var subQ1=sQuery(id+"F0.wireOp",EDGE,"E5");var subQ2=sQuery(id+"F0.wireOp",EDGE,"E4");Q27=makeQuery(id+"F3.opBoolean","SPLIT",EDGE,{"disambiguationData":[TD([makeQuery(id+"F1.opExtrude","SWEPT_FACE",FACE,{"disambiguationData":[OSD([subQ2])]})])],"derivedFrom":makeQuery(id+"F2.opPattern","COPY",EDGE,{"derivedFrom":makeQuery(id+"F1.opExtrude","CAP_EDGE",EDGE,{"disambiguationData":[OSD([subQ1])],"isStart":true}),"instanceName":"3"})});}
            fillet(context, id + "F6", {"entities" : qUnion([Q0, Q1, Q2, Q3, Q4, Q5, Q6, Q7, Q8, Q9, Q10, Q11, Q12, Q13, Q14, Q15, Q16, Q17, Q18, Q19, Q20, Q21, Q22, Q23, Q24, Q25, Q26, Q27]), "radius" : 1.5 * mm, "tangentPropagation" : true, "allowEdgeOverflow" : false});
        }
        {
            var Q0;
            {var subQ4=sQuery(id+"F0.wireOp",EDGE,"E7");var subQ5=sQuery(id+"F0.wireOp",EDGE,"E6");Q0=makeQuery(id+"F3.opBoolean","SPLIT",EDGE,{"disambiguationData":[TD([makeQuery(id+"F2.opPattern","COPY",FACE,{"derivedFrom":makeQuery(id+"F1.opExtrude","SWEPT_FACE",FACE,{"disambiguationData":[OSD([subQ4])]}),"instanceName":"3"})])],"derivedFrom":makeQuery(id+"F2.opPattern","COPY",EDGE,{"derivedFrom":makeQuery(id+"F1.opExtrude","CAP_EDGE",EDGE,{"disambiguationData":[OSD([subQ5])],"isStart":true}),"instanceName":"4"})});}
            var Q1;
            {var subQ4=sQuery(id+"F0.wireOp",EDGE,"E7");var subQ5=sQuery(id+"F0.wireOp",EDGE,"E6");Q1=makeQuery(id+"F3.opBoolean","SPLIT",EDGE,{"disambiguationData":[TD([makeQuery(id+"F2.opPattern","COPY",FACE,{"derivedFrom":makeQuery(id+"F1.opExtrude","SWEPT_FACE",FACE,{"disambiguationData":[OSD([subQ5])]}),"instanceName":"4"})])],"derivedFrom":makeQuery(id+"F2.opPattern","COPY",EDGE,{"derivedFrom":makeQuery(id+"F1.opExtrude","CAP_EDGE",EDGE,{"disambiguationData":[OSD([subQ4])],"isStart":true}),"instanceName":"3"})});}
            var Q2;
            {var subQ0=sQuery(id+"F0.wireOp",EDGE,"E2");var subQ1=makeQuery(id+"F1.opExtrude","CAP_EDGE",EDGE,{"disambiguationData":[OSD([subQ0]),TDD([makeQuery(id+"F0.imprint","IMPRINT",EDGE,{"disambiguationData":[TD([[makeQuery(id+"F0.imprint","INTERSECT",VERTEX,{"disambiguationData":[OD(0.0)],"derivedFrom":[subQ0,sQuery(id+"F0.wireOp",EDGE,"E4")]}),-1.0]])],"derivedFrom":subQ0})])],"isStart":true});Q2=makeQuery(id+"F3.opBoolean","MERGE",EDGE,{"derivedFrom":[subQ1,makeQuery(id+"F2.opPattern","COPY",EDGE,{"derivedFrom":subQ1,"instanceName":"1"})]});}
            var Q3;
            {var subQ0=sQuery(id+"F0.wireOp",EDGE,"E7");var subQ1=sQuery(id+"F0.wireOp",EDGE,"E6");Q3=makeQuery(id+"F3.opBoolean","SPLIT",EDGE,{"disambiguationData":[TD([makeQuery(id+"F2.opPattern","COPY",FACE,{"derivedFrom":makeQuery(id+"F1.opExtrude","SWEPT_FACE",FACE,{"disambiguationData":[OSD([subQ1])]}),"instanceName":"3"})])],"derivedFrom":makeQuery(id+"F2.opPattern","COPY",EDGE,{"derivedFrom":makeQuery(id+"F1.opExtrude","CAP_EDGE",EDGE,{"disambiguationData":[OSD([subQ0])],"isStart":true}),"instanceName":"2"})});}
            var Q4;
            {var subQ0=sQuery(id+"F0.wireOp",EDGE,"E7");var subQ3=sQuery(id+"F0.wireOp",EDGE,"E4");var subQ4=sQuery(id+"F0.wireOp",EDGE,"E2");var subQ6=makeQuery(id+"F0.imprint","IMPRINT",EDGE,{"disambiguationData":[TD([[makeQuery(id+"F0.imprint","INTERSECT",VERTEX,{"disambiguationData":[OD(0.0)],"derivedFrom":[subQ4,subQ3]}),-1.0]])],"derivedFrom":subQ4});Q4=makeQuery(id+"F3.opBoolean","SPLIT",EDGE,{"disambiguationData":[TD([makeQuery(id+"F2.opPattern","COPY",FACE,{"derivedFrom":makeQuery(id+"F1.opExtrude","SWEPT_FACE",FACE,{"disambiguationData":[OSD([subQ0])]}),"instanceName":"2"})])],"derivedFrom":makeQuery(id+"F1.opExtrude","CAP_EDGE",EDGE,{"disambiguationData":[OSD([subQ4]),TDD([subQ6])],"isStart":true})});}
            var Q5;
            {var subQ0=sQuery(id+"F0.wireOp",EDGE,"E7");var subQ1=sQuery(id+"F0.wireOp",EDGE,"E6");Q5=makeQuery(id+"F3.opBoolean","SPLIT",EDGE,{"disambiguationData":[TD([makeQuery(id+"F2.opPattern","COPY",FACE,{"derivedFrom":makeQuery(id+"F1.opExtrude","SWEPT_FACE",FACE,{"disambiguationData":[OSD([subQ0])]}),"instanceName":"2"})])],"derivedFrom":makeQuery(id+"F2.opPattern","COPY",EDGE,{"derivedFrom":makeQuery(id+"F1.opExtrude","CAP_EDGE",EDGE,{"disambiguationData":[OSD([subQ1])],"isStart":true}),"instanceName":"3"})});}
            var Q6;
            {var subQ0=sQuery(id+"F0.wireOp",EDGE,"E7");var subQ1=sQuery(id+"F0.wireOp",EDGE,"E6");Q6=makeQuery(id+"F3.opBoolean","SPLIT",EDGE,{"disambiguationData":[TD([makeQuery(id+"F2.opPattern","COPY",FACE,{"derivedFrom":makeQuery(id+"F1.opExtrude","SWEPT_FACE",FACE,{"disambiguationData":[OSD([subQ1])]}),"instanceName":"2"})])],"derivedFrom":makeQuery(id+"F2.opPattern","COPY",EDGE,{"derivedFrom":makeQuery(id+"F1.opExtrude","CAP_EDGE",EDGE,{"disambiguationData":[OSD([subQ0])],"isStart":true}),"instanceName":"1"})});}
            var Q7;
            {var subQ0=sQuery(id+"F0.wireOp",EDGE,"E7");var subQ1=sQuery(id+"F0.wireOp",EDGE,"E6");Q7=makeQuery(id+"F3.opBoolean","SPLIT",EDGE,{"disambiguationData":[TD([makeQuery(id+"F2.opPattern","COPY",FACE,{"derivedFrom":makeQuery(id+"F1.opExtrude","SWEPT_FACE",FACE,{"disambiguationData":[OSD([subQ0])]}),"instanceName":"1"})])],"derivedFrom":makeQuery(id+"F2.opPattern","COPY",EDGE,{"derivedFrom":makeQuery(id+"F1.opExtrude","CAP_EDGE",EDGE,{"disambiguationData":[OSD([subQ1])],"isStart":true}),"instanceName":"2"})});}
            var Q8;
            {var subQ0=sQuery(id+"F0.wireOp",EDGE,"E7");var subQ3=sQuery(id+"F0.wireOp",EDGE,"E4");var subQ4=sQuery(id+"F0.wireOp",EDGE,"E2");var subQ6=makeQuery(id+"F0.imprint","IMPRINT",EDGE,{"disambiguationData":[TD([[makeQuery(id+"F0.imprint","INTERSECT",VERTEX,{"disambiguationData":[OD(0.0)],"derivedFrom":[subQ4,subQ3]}),-1.0]])],"derivedFrom":subQ4});Q8=makeQuery(id+"F3.opBoolean","SPLIT",EDGE,{"disambiguationData":[TD([makeQuery(id+"F2.opPattern","COPY",FACE,{"derivedFrom":makeQuery(id+"F1.opExtrude","SWEPT_FACE",FACE,{"disambiguationData":[OSD([subQ0])]}),"instanceName":"1"})])],"derivedFrom":makeQuery(id+"F1.opExtrude","CAP_EDGE",EDGE,{"disambiguationData":[OSD([subQ4]),TDD([subQ6])],"isStart":true})});}
            var Q9;
            {var subQ0=sQuery(id+"F0.wireOp",EDGE,"E7");var subQ2=sQuery(id+"F0.wireOp",EDGE,"E2");var subQ4=makeQuery(id+"F0.imprint","IMPRINT",EDGE,{"disambiguationData":[TD([[makeQuery(id+"F0.imprint","INTERSECT",VERTEX,{"derivedFrom":[subQ2,subQ0]}),-1.0]])],"derivedFrom":subQ2});Q9=makeQuery(id+"F3.opBoolean","SPLIT",EDGE,{"disambiguationData":[TD([makeQuery(id+"F1.opExtrude","SWEPT_FACE",FACE,{"disambiguationData":[OSD([subQ0])]})])],"derivedFrom":makeQuery(id+"F1.opExtrude","CAP_EDGE",EDGE,{"disambiguationData":[OSD([subQ2]),TDD([subQ4])],"isStart":true})});}
            var Q10;
            {var subQ0=sQuery(id+"F0.wireOp",EDGE,"E7");var subQ1=sQuery(id+"F0.wireOp",EDGE,"E6");Q10=makeQuery(id+"F3.opBoolean","SPLIT",EDGE,{"disambiguationData":[TD([makeQuery(id+"F2.opPattern","COPY",FACE,{"derivedFrom":makeQuery(id+"F1.opExtrude","SWEPT_FACE",FACE,{"disambiguationData":[OSD([subQ1])]}),"instanceName":"1"})])],"derivedFrom":makeQuery(id+"F1.opExtrude","CAP_EDGE",EDGE,{"disambiguationData":[OSD([subQ0])],"isStart":true})});}
            var Q11;
            {var subQ0=sQuery(id+"F0.wireOp",EDGE,"E7");var subQ1=sQuery(id+"F0.wireOp",EDGE,"E6");Q11=makeQuery(id+"F3.opBoolean","SPLIT",EDGE,{"disambiguationData":[TD([makeQuery(id+"F1.opExtrude","SWEPT_FACE",FACE,{"disambiguationData":[OSD([subQ0])]})])],"derivedFrom":makeQuery(id+"F2.opPattern","COPY",EDGE,{"derivedFrom":makeQuery(id+"F1.opExtrude","CAP_EDGE",EDGE,{"disambiguationData":[OSD([subQ1])],"isStart":true}),"instanceName":"1"})});}
            var Q12;
            {var subQ0=sQuery(id+"F0.wireOp",EDGE,"E7");var subQ1=sQuery(id+"F0.wireOp",EDGE,"E6");Q12=makeQuery(id+"F3.opBoolean","SPLIT",EDGE,{"disambiguationData":[TD([makeQuery(id+"F2.opPattern","COPY",FACE,{"derivedFrom":makeQuery(id+"F1.opExtrude","SWEPT_FACE",FACE,{"disambiguationData":[OSD([subQ0])]}),"instanceName":"4"})])],"derivedFrom":makeQuery(id+"F1.opExtrude","CAP_EDGE",EDGE,{"disambiguationData":[OSD([subQ1])],"isStart":true})});}
            var Q13;
            {var subQ0=sQuery(id+"F0.wireOp",EDGE,"E7");var subQ1=sQuery(id+"F0.wireOp",EDGE,"E6");var subQ2=sQuery(id+"F0.wireOp",EDGE,"E2");var subQ4=makeQuery(id+"F0.imprint","IMPRINT",EDGE,{"disambiguationData":[TD([[makeQuery(id+"F0.imprint","INTERSECT",VERTEX,{"derivedFrom":[subQ2,subQ0]}),-1.0]])],"derivedFrom":subQ2});Q13=makeQuery(id+"F3.opBoolean","SPLIT",EDGE,{"disambiguationData":[TD([makeQuery(id+"F1.opExtrude","SWEPT_FACE",FACE,{"disambiguationData":[OSD([subQ1])]})])],"derivedFrom":makeQuery(id+"F1.opExtrude","CAP_EDGE",EDGE,{"disambiguationData":[OSD([subQ2]),TDD([subQ4])],"isStart":true})});}
            var Q14;
            {var subQ0=sQuery(id+"F0.wireOp",EDGE,"E7");var subQ1=sQuery(id+"F0.wireOp",EDGE,"E6");Q14=makeQuery(id+"F3.opBoolean","SPLIT",EDGE,{"disambiguationData":[TD([makeQuery(id+"F1.opExtrude","SWEPT_FACE",FACE,{"disambiguationData":[OSD([subQ1])]})])],"derivedFrom":makeQuery(id+"F2.opPattern","COPY",EDGE,{"derivedFrom":makeQuery(id+"F1.opExtrude","CAP_EDGE",EDGE,{"disambiguationData":[OSD([subQ0])],"isStart":true}),"instanceName":"4"})});}
            fillet(context, id + "F7", {"entities" : qUnion([Q0, Q1, Q2, Q3, Q4, Q5, Q6, Q7, Q8, Q9, Q10, Q11, Q12, Q13, Q14]), "radius" : 1.2 * mm, "tangentPropagation" : true, "allowEdgeOverflow" : false});
        }
    });
